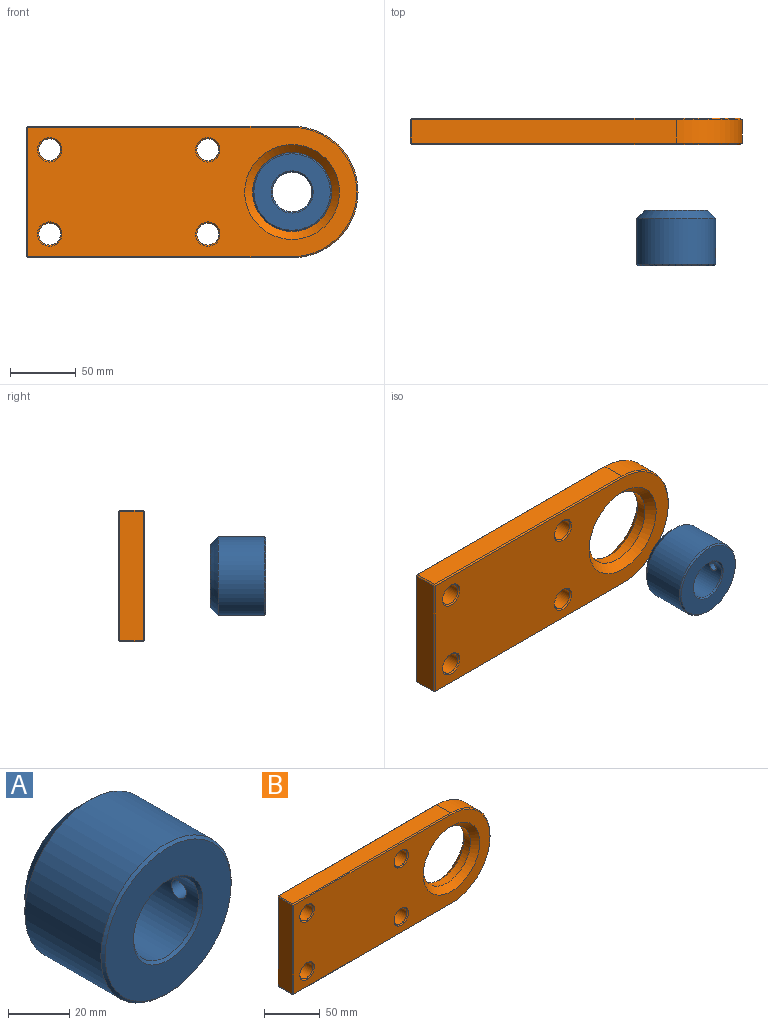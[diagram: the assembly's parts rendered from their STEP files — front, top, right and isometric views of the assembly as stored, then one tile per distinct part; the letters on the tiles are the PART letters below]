
ASSEMBLY  parts=2 mates=1
PART A: 10 faces, bbox 60x42x60 mm
  f0: cylinder r=15mm len=40mm, axis (0,1,0), area 3733.2mm2, adj f4,f6,f8
  f1: cylinder r=30mm len=60mm, axis (0,1,0), area 6538.5mm2, adj f5,f7,f9
  f2: plane 58x58mm, normal (0,-1,0), area 1837.8mm2, adj f4,f5
  f3: plane 48x48mm, normal (0,1,0), area 1005.3mm2, adj f6,f7
  f4: cone r=15mm half-angle=45deg, axis (0,-1,0), area 137.7mm2, adj f0,f2
  f5: cone r=29mm half-angle=45deg, axis (0,1,0), area 262.1mm2, adj f1,f2
  f6: cone r=16mm half-angle=45deg, axis (0,1,0), area 137.7mm2, adj f0,f3
  f7: cone r=30mm half-angle=45deg, axis (0,-1,0), area 1439.5mm2, adj f1,f3
  f8: cylinder r=3.4mm len=14.18mm, axis (-1,0,0), area 302.9mm2, adj f0,f9
  f9: bspline ~8.85x8.59mm, area 31.9mm2, adj f1,f8
PART B: 35 faces, bbox 252x20x100 mm
  f0: cylinder r=50mm len=100mm, axis (0,1,0), area 2827.4mm2, adj f1,f8,f13,f26
  f1: plane 201x18mm, normal (0,0,1), area 3618mm2, adj f0,f15,f20,f25
  f2: plane 98x18mm, normal (-1,0,0), area 1764mm2, adj f16,f19,f20,f21
  f3: cylinder r=8.25mm len=18mm, axis (0,1,0), area 933.1mm2, adj f29,f33
  f4: cylinder r=8.25mm len=18mm, axis (0,1,0), area 933.1mm2, adj f30,f34
  f5: cylinder r=8.25mm len=18mm, axis (0,1,0), area 933.1mm2, adj f28,f32
  f6: cylinder r=8.25mm len=18mm, axis (0,1,0), area 933.1mm2, adj f27,f31
  f7: cylinder r=30mm len=60mm, axis (0,1,0), area 1508mm2, adj f11,f12
  f8: plane 201x18mm, normal (0,0,-1), area 3618mm2, adj f0,f14,f19,f24
  f9: plane 250x98mm, normal (0,-1,0), area 18322.8mm2, adj f12,f13,f14,f15,f16,f31,f32,f33
  f10: plane 250x98mm, normal (0,1,0), area 18322.8mm2, adj f11,f21,f24,f25,f26,f27,f28,f29
  f11: cone r=36mm half-angle=45deg, axis (0,1,0), area 1759.4mm2, adj f7,f10
  f12: cone r=30mm half-angle=45deg, axis (0,-1,0), area 1759.4mm2, adj f7,f9
  f13: cone r=49mm half-angle=45deg, axis (0,1,0), area 219.9mm2, adj f0,f9,f14,f15
  f14: plane 201x1mm, normal (0,-0.71,-0.71), area 284.3mm2, adj f8,f9,f13,f17
  f15: plane 201x1mm, normal (0,-0.71,0.71), area 284.3mm2, adj f1,f9,f13,f18
  f16: plane 98x1mm, normal (-0.71,-0.71,0), area 138.6mm2, adj f2,f9,f17,f18
  f17: plane 1x1mm, normal (-0.58,-0.58,-0.58), area 0.9mm2, adj f14,f16,f19
  f18: plane 1x1mm, normal (-0.58,-0.58,0.58), area 0.9mm2, adj f15,f16,f20
  f19: plane 18x1mm, normal (-0.71,0,-0.71), area 25.5mm2, adj f2,f8,f17,f22
  f20: plane 18x1mm, normal (-0.71,0,0.71), area 25.5mm2, adj f1,f2,f18,f23
  f21: plane 98x1mm, normal (-0.71,0.71,0), area 138.6mm2, adj f2,f10,f22,f23
  f22: plane 1x1mm, normal (-0.58,0.58,-0.58), area 0.9mm2, adj f19,f21,f24
  f23: plane 1x1mm, normal (-0.58,0.58,0.58), area 0.9mm2, adj f20,f21,f25
  f24: plane 201x1mm, normal (0,0.71,-0.71), area 284.3mm2, adj f8,f10,f22,f26
  f25: plane 201x1mm, normal (0,0.71,0.71), area 284.3mm2, adj f1,f10,f23,f26
  f26: cone r=50mm half-angle=45deg, axis (0,-1,0), area 219.9mm2, adj f0,f10,f24,f25
  f27: cone r=9.25mm half-angle=45deg, axis (0,1,0), area 77.8mm2, adj f6,f10
  f28: cone r=9.25mm half-angle=45deg, axis (0,1,0), area 77.8mm2, adj f5,f10
  f29: cone r=9.25mm half-angle=45deg, axis (0,1,0), area 77.8mm2, adj f3,f10
  f30: cone r=9.25mm half-angle=45deg, axis (0,1,0), area 77.8mm2, adj f4,f10
  f31: cone r=8.25mm half-angle=45deg, axis (0,-1,0), area 77.8mm2, adj f6,f9
  f32: cone r=8.25mm half-angle=45deg, axis (0,-1,0), area 77.8mm2, adj f5,f9
  f33: cone r=8.25mm half-angle=45deg, axis (0,-1,0), area 77.8mm2, adj f3,f9
  f34: cone r=8.25mm half-angle=45deg, axis (0,-1,0), area 77.8mm2, adj f4,f9
PLACE A t=(68.97,-55.28,13.18)mm
PLACE B t=(-7.03,14.72,13.18)mm
MATE fastened A.f0 <-> B.f7  axis (0,1,0) through (68.97,-55.28,13.18)mm
